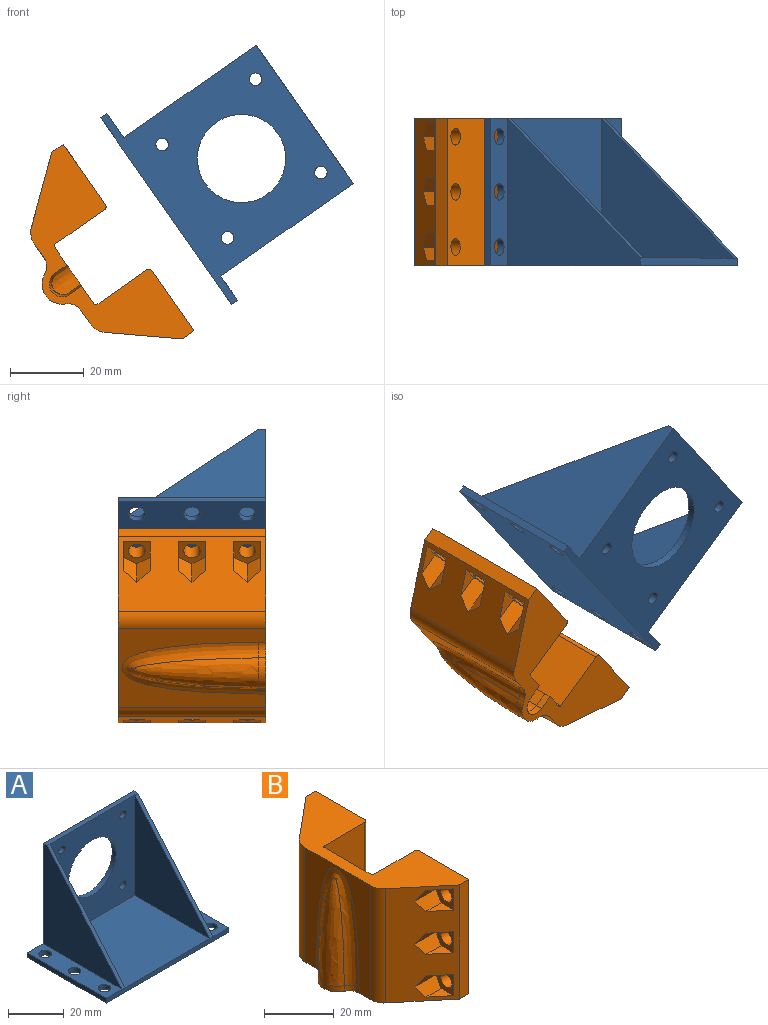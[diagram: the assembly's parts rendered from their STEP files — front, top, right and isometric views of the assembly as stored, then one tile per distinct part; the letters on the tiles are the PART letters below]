
ASSEMBLY  parts=2 mates=3
PART A: 27 faces, bbox 62x40x46 mm
  f0: plane 43x38mm, normal (0,0,1), area 1634mm2, adj f2,f4,f24,f26
  f1: plane 40x8mm, normal (0,0,1), area 272.3mm2, adj f4,f5,f8,f9,f11,f12,f15
  f2: plane 44x43mm, normal (0,-1,0), area 1403.3mm2, adj f0,f17,f18,f19,f20,f21,f22,f24
  f3: plane 40x2mm, normal (-1,0,0), area 80mm2, adj f4,f12,f13,f14
  f4: plane 62x2mm, normal (0,-1,0), area 124mm2, adj f0,f1,f3,f5,f13,f14,f23,f25
  f5: plane 40x2mm, normal (1,0,0), area 80mm2, adj f1,f4,f12,f14
  f6: cylinder r=2.25mm len=4.5mm, axis (0,0,-1), area 28.3mm2, adj f13,f14
  f7: cylinder r=2.25mm len=4.5mm, axis (0,0,-1), area 28.3mm2, adj f13,f14
  f8: cylinder r=2.25mm len=4.5mm, axis (0,0,-1), area 28.3mm2, adj f1,f14
  f9: cylinder r=2.25mm len=4.5mm, axis (0,0,-1), area 28.3mm2, adj f1,f14
  f10: cylinder r=2.25mm len=4.5mm, axis (0,0,-1), area 28.3mm2, adj f13,f14
  f11: cylinder r=2.25mm len=4.5mm, axis (0,0,-1), area 28.3mm2, adj f1,f14
  f12: plane 62x46mm, normal (0,1,0), area 1659.3mm2, adj f1,f3,f5,f13,f14,f15,f16,f17
  f13: plane 40x8mm, normal (0,0,1), area 272.3mm2, adj f3,f4,f6,f7,f10,f12,f16
  f14: plane 62x40mm, normal (0,0,-1), area 2384.6mm2, adj f3,f4,f5,f6,f7,f8,f9,f10
  f15: plane 44x40mm, normal (1,0,0), area 924mm2, adj f1,f12,f22,f23
  f16: plane 44x40mm, normal (-1,0,0), area 924mm2, adj f12,f13,f22,f25
  f17: cylinder r=12mm len=24mm, axis (0,1,0), area 150.8mm2, adj f2,f12
  f18: cylinder r=1.7mm len=3.4mm, axis (0,1,0), area 21.4mm2, adj f2,f12
  f19: cylinder r=1.7mm len=3.4mm, axis (0,1,0), area 21.4mm2, adj f2,f12
  f20: cylinder r=1.7mm len=3.4mm, axis (0,1,0), area 21.4mm2, adj f2,f12
  f21: cylinder r=1.7mm len=3.4mm, axis (0,1,0), area 21.4mm2, adj f2,f12
  f22: plane 46x2mm, normal (0,0,1), area 92mm2, adj f2,f12,f15,f16,f23,f25
  f23: plane 44x38mm, normal (0,-0.76,0.65), area 87.2mm2, adj f4,f15,f22,f24
  f24: plane 44x38mm, normal (-1,0,0), area 836mm2, adj f0,f2,f23
  f25: plane 44x38mm, normal (0,-0.76,0.65), area 87.2mm2, adj f4,f16,f22,f26
  f26: plane 44x38mm, normal (1,0,0), area 836mm2, adj f0,f2,f25
PART B: 67 faces, bbox 27.5x62x40.9 mm
  f0: plane 40x19mm, normal (1,0,0), area 626.2mm2, adj f6,f7,f16,f17,f62,f63,f64,f65
  f1: plane 40x26.51mm, normal (-1,0,0), area 504mm2, adj f12,f13,f16,f17,f59,f60,f61
  f2: plane 40x16.22mm, normal (-0.64,0.77,0), area 629.5mm2, adj f11,f12,f16,f17,f24,f25,f26,f27
  f3: plane 40x16.22mm, normal (-0.64,-0.77,0), area 629.5mm2, adj f13,f14,f16,f17,f39,f40,f41,f42
  f4: cylinder r=1mm len=40mm, axis (0,0,1), area 62.8mm2, adj f5,f15,f16,f17
  f5: plane 40x16.5mm, normal (0,1,0), area 660mm2, adj f4,f6,f16,f17
  f6: cylinder r=0.5mm len=40mm, axis (0,0,1), area 31.4mm2, adj f0,f5,f16,f17
  f7: cylinder r=0.5mm len=40mm, axis (0,0,1), area 31.4mm2, adj f0,f8,f16,f17
  f8: plane 40x16.5mm, normal (0,-1,0), area 660mm2, adj f7,f9,f16,f17
  f9: cylinder r=1mm len=40mm, axis (0,0,1), area 62.8mm2, adj f8,f10,f16,f17
  f10: plane 40x20mm, normal (1,0,0), area 752.3mm2, adj f9,f11,f16,f17,f21,f22,f23
  f11: plane 40x3.8mm, normal (0,1,0), area 152mm2, adj f2,f10,f16,f17
  f12: cylinder r=5.5mm len=40mm, axis (0,0,1), area 192.7mm2, adj f1,f2,f16,f17
  f13: cylinder r=5.5mm len=40mm, axis (0,0,1), area 192.7mm2, adj f1,f3,f16,f17
  f14: plane 40x3.8mm, normal (0,-1,0), area 152mm2, adj f3,f15,f16,f17
  f15: plane 40x20mm, normal (1,0,0), area 752.3mm2, adj f4,f14,f16,f17,f18,f19,f20
  f16: plane 62x27.52mm, normal (0,0,-1), area 729.5mm2, adj f0,f1,f2,f3,f4,f5,f6,f7
  f17: plane 62x22mm, normal (0,0,1), area 725.8mm2, adj f0,f1,f2,f3,f4,f5,f6,f7
  f18: cylinder r=2.25mm len=5mm, axis (1,0,0), area 70.7mm2, adj f15,f49
  f19: cylinder r=2.25mm len=5mm, axis (1,0,0), area 70.7mm2, adj f15,f44
  f20: cylinder r=2.25mm len=5mm, axis (1,0,0), area 70.7mm2, adj f15,f39
  f21: cylinder r=2.25mm len=5mm, axis (1,0,0), area 70.7mm2, adj f10,f34
  f22: cylinder r=2.25mm len=5mm, axis (1,0,0), area 70.7mm2, adj f10,f29
  f23: cylinder r=2.25mm len=5mm, axis (1,0,0), area 70.7mm2, adj f10,f24
  f24: plane 7.4x7.27mm, normal (-1,0,0), area 30mm2, adj f2,f23,f25,f26,f27,f28
  f25: plane 6.16x5.14mm, normal (0,0,1), area 15.8mm2, adj f2,f24,f26
  f26: plane 8.73x3.7mm, normal (0,0.87,0.5), area 31.8mm2, adj f2,f24,f25,f27
  f27: plane 8.73x3.7mm, normal (0,0.87,-0.5), area 31.8mm2, adj f2,f24,f26,f28
  f28: plane 6.16x5.14mm, normal (0,0,-1), area 15.8mm2, adj f2,f24,f27
  f29: plane 7.4x7.27mm, normal (-1,0,0), area 30mm2, adj f2,f22,f30,f31,f32,f33
  f30: plane 6.16x5.14mm, normal (0,0,1), area 15.8mm2, adj f2,f29,f31
  f31: plane 8.73x3.7mm, normal (0,0.87,0.5), area 31.8mm2, adj f2,f29,f30,f32
  f32: plane 8.73x3.7mm, normal (0,0.87,-0.5), area 31.8mm2, adj f2,f29,f31,f33
  f33: plane 6.16x5.14mm, normal (0,0,-1), area 15.8mm2, adj f2,f29,f32
  f34: plane 7.4x7.27mm, normal (-1,0,0), area 30mm2, adj f2,f21,f35,f36,f37,f38
  f35: plane 6.16x5.14mm, normal (0,0,1), area 15.8mm2, adj f2,f34,f36
  f36: plane 8.73x3.7mm, normal (0,0.87,0.5), area 31.8mm2, adj f2,f34,f35,f37
  f37: plane 8.73x3.7mm, normal (0,0.87,-0.5), area 31.8mm2, adj f2,f34,f36,f38
  f38: plane 6.16x5.14mm, normal (0,0,-1), area 15.8mm2, adj f2,f34,f37
  f39: plane 7.4x7.27mm, normal (-1,0,0), area 30mm2, adj f3,f20,f40,f41,f42,f43
  f40: plane 6.16x5.14mm, normal (0,0,1), area 15.8mm2, adj f3,f39,f41
  f41: plane 8.73x3.7mm, normal (0,-0.87,0.5), area 31.8mm2, adj f3,f39,f40,f42
  f42: plane 8.73x3.7mm, normal (0,-0.87,-0.5), area 31.8mm2, adj f3,f39,f41,f43
  f43: plane 6.16x5.14mm, normal (0,0,-1), area 15.8mm2, adj f3,f39,f42
  f44: plane 7.4x7.27mm, normal (-1,0,0), area 30mm2, adj f3,f19,f45,f46,f47,f48
  f45: plane 6.16x5.14mm, normal (0,0,1), area 15.8mm2, adj f3,f44,f46
  f46: plane 8.73x3.7mm, normal (0,-0.87,0.5), area 31.8mm2, adj f3,f44,f45,f47
  f47: plane 8.73x3.7mm, normal (0,-0.87,-0.5), area 31.8mm2, adj f3,f44,f46,f48
  f48: plane 6.16x5.14mm, normal (0,0,-1), area 15.8mm2, adj f3,f44,f47
  f49: plane 7.4x7.27mm, normal (-1,0,0), area 30mm2, adj f3,f18,f50,f51,f52,f53
  f50: plane 6.16x5.14mm, normal (0,0,1), area 15.8mm2, adj f3,f49,f51
  f51: plane 8.73x3.7mm, normal (0,-0.87,0.5), area 31.8mm2, adj f3,f49,f50,f52
  f52: plane 8.73x3.7mm, normal (0,-0.87,-0.5), area 31.8mm2, adj f3,f49,f51,f53
  f53: plane 6.16x5.14mm, normal (0,0,-1), area 15.8mm2, adj f3,f49,f52
  f54: cone r=0mm half-angle=11.8deg, axis (0,0,-1), area 0mm2, adj f58,f66
  f55: revolved ~34.39x10.01mm, area 226.5mm2, adj f56,f61
  f56: cylinder r=5.52mm len=10.01mm, axis (0,0,-1), area 25.1mm2, adj f16,f55,f59,f60,f61
  f57: cylinder r=3.5mm len=7mm, axis (0,0,-1), area 22mm2, adj f16,f58,f62,f63
  f58: cone r=2.99mm half-angle=1.6deg, axis (0,0,-1), area 181.3mm2, adj f54,f57,f64,f65
  f59: cylinder r=4mm len=3.63mm, axis (0,0,-1), area 9.2mm2, adj f1,f16,f56,f61
  f60: cylinder r=4mm len=3.63mm, axis (0,0,-1), area 9.2mm2, adj f1,f16,f56,f61
  f61: bspline ~39.99x17.39mm, area 312.6mm2, adj f1,f55,f56,f59,f60
  f62: plane 4x2mm, normal (0,-1,0), area 8mm2, adj f0,f16,f57,f65
  f63: plane 4x2mm, normal (0,1,0), area 8mm2, adj f0,f16,f57,f64
  f64: plane 17.77x4mm, normal (0,1,-0.03), area 71.1mm2, adj f0,f58,f63,f66
  f65: plane 17.77x4mm, normal (0,-1,-0.03), area 71.1mm2, adj f0,f58,f62,f66
  f66: bspline ~6.96x5.99mm, area 39.8mm2, adj f0,f54,f64,f65
PLACE A rot(axis=(0.46,0,0.89),180deg) t=(-28.83,0.43,-17.11)mm
PLACE B rot(axis=(-0.91,-0.29,-0.29),95.2deg) t=(-49.1,1.43,-31.3)mm
MATE cylindrical B.f19 <-> A.f8  axis (0.82,0,0.57) through (-58.65,-14.57,-5.03)mm
MATE cylindrical B.f21 <-> A.f6  axis (0.82,0,0.57) through (-25.63,-14.57,-47.83)mm
MATE parallel A.f14 <-> B.f15  axis (-0.82,0,-0.57) through (-28.83,0.43,-17.11)mm
